# Revit family: LAMP_BAZZ AIR ASYMMETRIC
name_source: partatom
category: Modelos genéricos
revit_build: Autodesk Revit 2018 (Build: 20190510_1515(x64)
units: mm (PartAtom-declared; Revit-internal decimal feet)

## family parameters
Anfitrión = Cara
Compartido = No
Corte con vacíos al cargar = No
Cota de conector redondo = Diámetro de uso
Puede alojar armadura = No
Punto de cálculo de habitación = No
Tipo de pieza = Normal

## types (8) — shared parameters
CRI = 80
Comentarios de tipo = Availability of tilting between 0º and 90º when placed in a project.
Dist. Rótula = 403 mm  [stored 1.32218 ft]
Elevación por defecto = 1219 mm
Fabricante = LAMP
Finish = Anodized matte black
Gear = Electronic
Height = 84 mm  [stored 0.275591 ft]
Installation instructions = http://www.lamp.es
Insulation class = I
LED Lifetime = 50.000 L80
Lamp = MID-POWER LED
Last update = 17/02/2022
Luminaire type = Outdoor -Recessed luminaire
MacAdam = <3
Manufacturer URL = http://www.lamp.es
Manufacturer country = Spain
Manufacturer name = LAMP
Model explanation = Availability of tilting between 0º and 90º when placed in a project.
Power Supply = 220-240V 50/60Hz
Product URL = http://www.lamp.es
Product datasheet = http://www.lamp.es
Protection rating = IP67 / IK10
Type = MID POWER SAMSUNG

## per-type parameters (varying)
| type | Descripción | Dimensions | Efficacy | Initial color | Initial intensity | Modelo | Photometric web file | Plum | Power | Product code | Weight |
| 1945LM 3000 1M | BAZZ AIR ASYM 1M 2100 WW BK. | 1043x106x84 | 94 lm/W | 3000 K | 1945 lm | BZ1SF100LOAS830NB | Bazz air asymmetric - base : 1945LM 3000 1M | 21 W | 19 W | BZ1SF100LOAS830NB | 3.73 kg |
| 2043LM 4000 1M | BAZZ AIR ASYM 1M 2100 NW BK. | 1043x106x84 | 99 lm/W | 4000 K | 2043 lm | BZ1SF100LOAS840NB | Bazz air asymmetric - base : 2043LM 4000 1M | 21 W | 19 W | BZ1SF100LOAS840NB | 3.73 kg |
| 3813LM 3000 1M | BAZZ AIR ASYM 1M 4200 WW BK. | 1043x106x84 | 95 lm/W | 3000 K | 3813 lm | BZ1SF100MOAS830NB | Bazz air asymmetric - base : 3813LM 3000 1M | 40 W | 37 W | BZ1SF100MOAS830NB | 3.93 kg |
| 4004LM 4000 1M | BAZZ AIR ASYM 2M 4200 WW BK. | 1043x106x84 | 97 lm/W | 3000 K | 3891 lm | BZ1SF200LOAS830NB | Bazz air asymmetric - base : 4004LM 4000 1M | 40 W | 38 W | BZ1SF200LOAS830NB | 6.70 kg |
| 3891LM 3000 2M | BAZZ AIR ASYM 1M 4200 NW BK. | 1043x106x84 | 100 lm/W | 4000 K | 4004 lm | BZ1SF100MOAS840NB | Bazz air asymmetric - base : 3891LM 3000 2M | 40 W | 37 W | BZ1SF100MOAS840NB | 3.93 kg |
| 4085LM 4000 2M | BAZZ AIR ASYM 2M 4200 NW BK. | 2036x106x84 | 102 lm/W | 4000 K | 4085 lm | BZ1SF200LOAS840NB | Bazz air asymmetric - base : 4085LM 4000 2M | 40 W | 38 W | BZ1SF200LOAS840NB | 6.70 kg |
| 7626LM 3000 2M | BAZZ AIR ASYM 2M 8100 WW BK. | 2036x106x84 | 99 lm/W | 3000 K | 7626 lm | BZ1SF200MOAS830NB | Bazz air asymmetric - base : 7626LM 3000 2M | 77 W | 75 W | BZ1SF200MOAS830NB | 6.70 kg |
| 8008LM 4000 2M | BAZZ AIR ASYM 2M 8100 NW BK. | 2036x106x84 | 104 lm/W | 4000 K | 8008 lm | BZ1SF200MOAS840NB | Bazz air asymmetric - base : 8008LM 4000 2M | 77 W | 75 W | BZ1SF200MOAS840NB | 6.70 kg |

note: [stored X ft] marks values corroborated as IEEE doubles in the binary element streams (Revit-internal decimal feet)

## geometry (parser evidence)
native form markers: Blend x2
no freeform markers — native parametric forms only
